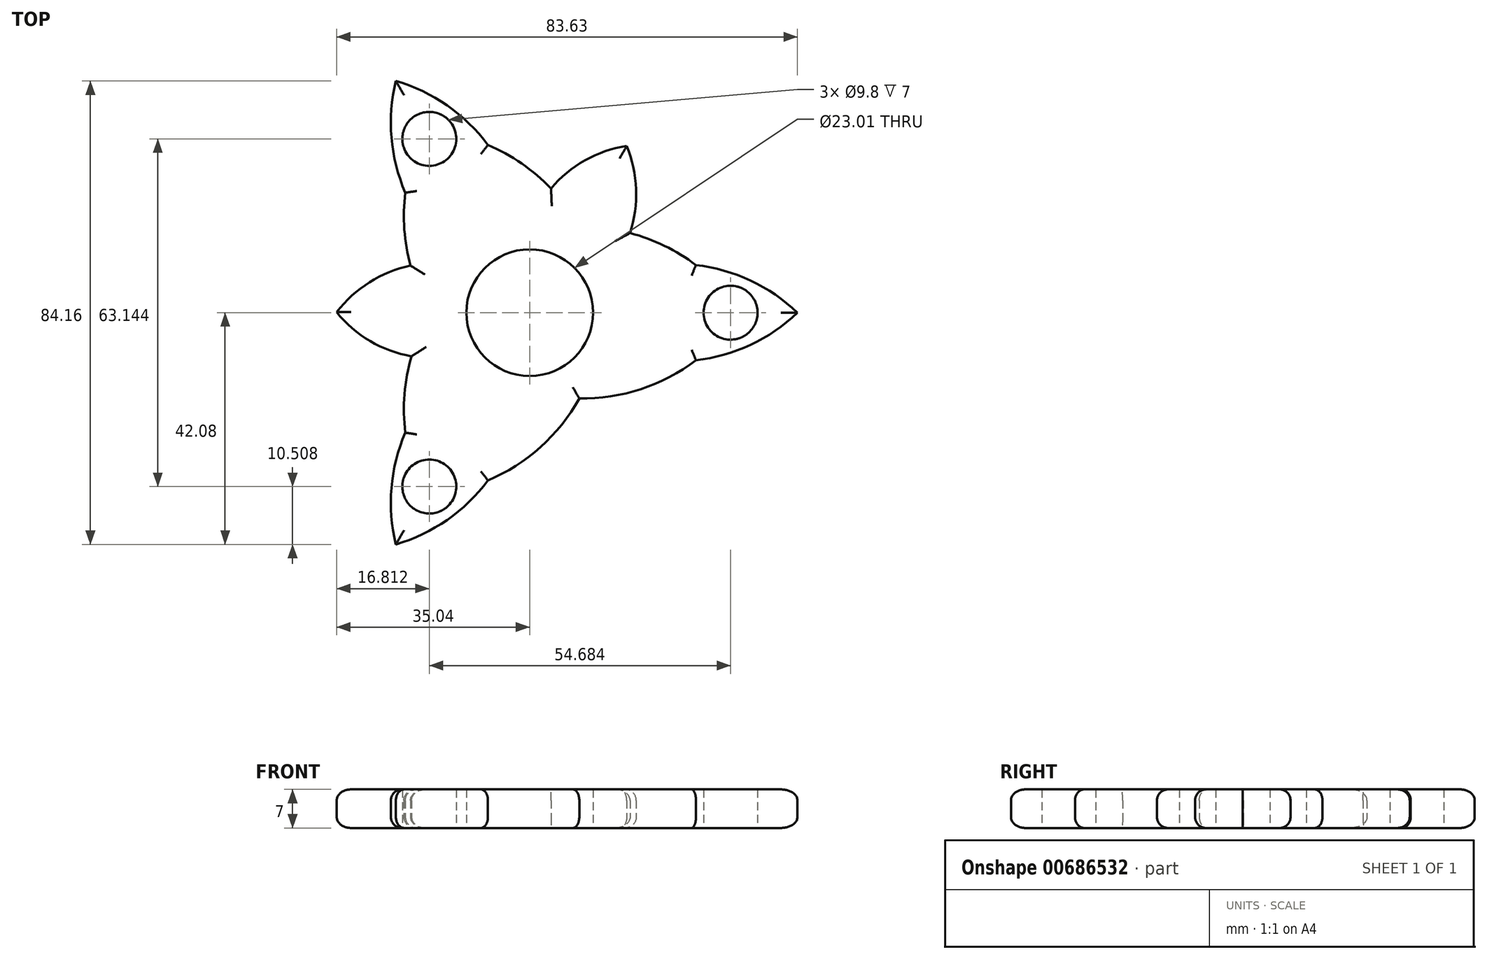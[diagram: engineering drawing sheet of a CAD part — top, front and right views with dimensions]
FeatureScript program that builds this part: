
annotation { "Feature Type Name" : "Feature", "Feature Type Description" : "" }
export const myFeature = defineFeature(function(context is Context, id is Id, definition is map)
    precondition{}
    {
        {
            var Q0;
            Q0=qCreatedBy(makeId("Top.planeOp"),FACE);
            var sketch = newSketch(context, id + "F0", { "sketchPlane" : qUnion([Q0])});
            skCircle(sketch, "E0", {"center": v(0, 0) * mm, "radius": 11.5 * mm});
            skArc(sketch, "E1", {"start": v(30.17, 8.66) * mm, "mid": v(15.75, 15.02) * mm, "end": v(0, 14.24) * mm});
            skArc(sketch, "E2", {"start": v(48.6, 0) * mm, "mid": v(40.09, 5.83) * mm, "end": v(30.17, 8.66) * mm});
            skArc(sketch, "E3.MirrorCS", {"start": v(30.17, -8.66) * mm, "mid": v(15.75, -15.02) * mm, "end": v(0, -14.24) * mm});
            skArc(sketch, "E4.MirrorCS", {"start": v(48.6, 0) * mm, "mid": v(40.09, -5.83) * mm, "end": v(30.17, -8.66) * mm});
            skPoint(sketch, "E5.center", {"position": v(-1.4, 1.63) * mm});
            skArc(sketch, "E6", {"start": v(17.6, 30.3) * mm, "mid": v(8.42, 26.66) * mm, "end": v(1.7, 19.42) * mm});
            skArc(sketch, "E7", {"start": v(17.6, 12.8) * mm, "mid": v(19.33, 21.55) * mm, "end": v(17.6, 30.3) * mm});
            skPoint(sketch, "E8", {"position": v(5.15, 23.94) * mm});
            skPoint(sketch, "E9", {"position": v(18.22, 14.47) * mm});
            skCircle(sketch, "E10", {"center": v(36.46, 0) * mm, "radius": 4.9 * mm});
            skArc(sketch, "E11.1.0", {"start": v(-35.04, 0.1) * mm, "mid": v(-27.3, -6.04) * mm, "end": v(-17.67, -8.25) * mm});
            skArc(sketch, "E11.1.1", {"start": v(-19.89, 8.85) * mm, "mid": v(-28.33, 5.97) * mm, "end": v(-35.04, 0.1) * mm});
            skArc(sketch, "E11.1.2", {"start": v(-22.58, 21.8) * mm, "mid": v(-20.88, 6.13) * mm, "end": v(-12.33, -7.12) * mm});
            skArc(sketch, "E11.1.3", {"start": v(-7.59, 30.46) * mm, "mid": v(5.13, 21.14) * mm, "end": v(12.33, 7.12) * mm});
            skArc(sketch, "E11.1.4", {"start": v(-24.3, 42.08) * mm, "mid": v(-15, 37.63) * mm, "end": v(-7.59, 30.46) * mm});
            skArc(sketch, "E11.1.5", {"start": v(-24.3, 42.08) * mm, "mid": v(-25.1, 31.8) * mm, "end": v(-22.58, 21.8) * mm});
            skCircle(sketch, "E11.1.6", {"center": v(-18.23, 31.57) * mm, "radius": 4.9 * mm});
            skArc(sketch, "E11.2.0", {"start": v(17.43, -30.4) * mm, "mid": v(18.88, -20.62) * mm, "end": v(15.98, -11.18) * mm});
            skArc(sketch, "E11.2.1", {"start": v(2.28, -21.65) * mm, "mid": v(9, -27.52) * mm, "end": v(17.43, -30.4) * mm});
            skArc(sketch, "E11.2.2", {"start": v(-7.59, -30.46) * mm, "mid": v(5.13, -21.14) * mm, "end": v(12.33, -7.12) * mm});
            skArc(sketch, "E11.2.3", {"start": v(-22.58, -21.8) * mm, "mid": v(-20.88, -6.13) * mm, "end": v(-12.33, 7.12) * mm});
            skArc(sketch, "E11.2.4", {"start": v(-24.3, -42.08) * mm, "mid": v(-25.1, -31.8) * mm, "end": v(-22.58, -21.8) * mm});
            skArc(sketch, "E11.2.5", {"start": v(-24.3, -42.08) * mm, "mid": v(-15, -37.63) * mm, "end": v(-7.59, -30.46) * mm});
            skCircle(sketch, "E11.2.6", {"center": v(-18.23, -31.57) * mm, "radius": 4.9 * mm});
            skSolve(sketch);
        }
        {
            var Q0;
            Q0=makeQuery(id+"F0.imprint","IMPRINT",FACE,{"disambiguationData":[TD([[makeQuery(id+"F0.imprint","IMPRINT",EDGE,{"derivedFrom":sQuery(id+"F0.wireOp",EDGE,"E0")}),-1.0]])]});
            var Q1;
            {var subQ0=sQuery(id+"F0.wireOp",EDGE,"E7");var subQ1=sQuery(id+"F0.wireOp",EDGE,"E1");var subQ2=makeQuery(id+"F0.imprint","INTERSECT",VERTEX,{"derivedFrom":[subQ1,subQ0]});Q1=makeQuery(id+"F0.imprint","IMPRINT",FACE,{"disambiguationData":[TD([[makeQuery(id+"F0.imprint","IMPRINT",EDGE,{"disambiguationData":[TD([[subQ2,-1.0]])],"derivedFrom":subQ1}),-1.0]])]});}
            var Q2;
            {var subQ0=sQuery(id+"F0.wireOp",EDGE,"E11.1.1");var subQ1=sQuery(id+"F0.wireOp",EDGE,"E11.1.0");var subQ2=makeQuery(id+"F0.imprint","INTERSECT",VERTEX,{"derivedFrom":[subQ1,subQ0]});Q2=makeQuery(id+"F0.imprint","IMPRINT",FACE,{"disambiguationData":[TD([[makeQuery(id+"F0.imprint","IMPRINT",EDGE,{"disambiguationData":[TD([[subQ2,-1.0]])],"derivedFrom":subQ1}),1.0]])]});}
            var Q3;
            {var subQ0=sQuery(id+"F0.wireOp",EDGE,"E11.2.0");var subQ1=sQuery(id+"F0.wireOp",EDGE,"E3.MirrorCS");var subQ2=makeQuery(id+"F0.imprint","INTERSECT",VERTEX,{"derivedFrom":[subQ1,subQ0]});Q3=makeQuery(id+"F0.imprint","IMPRINT",FACE,{"disambiguationData":[TD([[makeQuery(id+"F0.imprint","IMPRINT",EDGE,{"disambiguationData":[TD([[subQ2,-1.0]])],"derivedFrom":subQ1}),1.0]])]});}
            extrude(context, id + "F1", {"entities" : qUnion([Q0, Q1, Q2, Q3]), "depth" : 7 * mm, "offsetDistance" : 25 * mm});
        }
        {
            var Q0;
            Q0=makeQuery(id+"F1.opExtrude","CAP_EDGE",EDGE,{"disambiguationData":[OSD([sQuery(id+"F0.wireOp",EDGE,"E1")])],"isStart":true});
            var Q1;
            Q1=makeQuery(id+"F1.opExtrude","CAP_EDGE",EDGE,{"disambiguationData":[OSD([sQuery(id+"F0.wireOp",EDGE,"E7")])],"isStart":true});
            var Q2;
            Q2=makeQuery(id+"F1.opExtrude","CAP_EDGE",EDGE,{"disambiguationData":[OSD([sQuery(id+"F0.wireOp",EDGE,"E6")])],"isStart":true});
            var Q3;
            Q3=makeQuery(id+"F1.opExtrude","CAP_EDGE",EDGE,{"disambiguationData":[OSD([sQuery(id+"F0.wireOp",EDGE,"E11.1.3")])],"isStart":true});
            var Q4;
            Q4=makeQuery(id+"F1.opExtrude","CAP_EDGE",EDGE,{"disambiguationData":[OSD([sQuery(id+"F0.wireOp",EDGE,"E11.1.4")])],"isStart":true});
            var Q5;
            Q5=makeQuery(id+"F1.opExtrude","CAP_EDGE",EDGE,{"disambiguationData":[OSD([sQuery(id+"F0.wireOp",EDGE,"E11.1.5")])],"isStart":true});
            var Q6;
            Q6=makeQuery(id+"F1.opExtrude","CAP_EDGE",EDGE,{"disambiguationData":[OSD([sQuery(id+"F0.wireOp",EDGE,"E11.1.2")])],"isStart":true});
            var Q7;
            Q7=makeQuery(id+"F1.opExtrude","CAP_EDGE",EDGE,{"disambiguationData":[OSD([sQuery(id+"F0.wireOp",EDGE,"E11.1.1")])],"isStart":true});
            var Q8;
            Q8=makeQuery(id+"F1.opExtrude","CAP_EDGE",EDGE,{"disambiguationData":[OSD([sQuery(id+"F0.wireOp",EDGE,"E11.1.0")])],"isStart":true});
            var Q9;
            Q9=makeQuery(id+"F1.opExtrude","CAP_EDGE",EDGE,{"disambiguationData":[OSD([sQuery(id+"F0.wireOp",EDGE,"E11.2.3")])],"isStart":true});
            var Q10;
            Q10=makeQuery(id+"F1.opExtrude","CAP_EDGE",EDGE,{"disambiguationData":[OSD([sQuery(id+"F0.wireOp",EDGE,"E11.2.4")])],"isStart":true});
            var Q11;
            Q11=makeQuery(id+"F1.opExtrude","CAP_EDGE",EDGE,{"disambiguationData":[OSD([sQuery(id+"F0.wireOp",EDGE,"E11.2.5")])],"isStart":true});
            var Q12;
            Q12=makeQuery(id+"F1.opExtrude","CAP_EDGE",EDGE,{"disambiguationData":[OSD([sQuery(id+"F0.wireOp",EDGE,"E11.2.2")])],"isStart":true});
            var Q13;
            Q13=makeQuery(id+"F1.opExtrude","CAP_EDGE",EDGE,{"disambiguationData":[OSD([sQuery(id+"F0.wireOp",EDGE,"E11.2.1")])],"isStart":true});
            var Q14;
            Q14=makeQuery(id+"F1.opExtrude","CAP_EDGE",EDGE,{"disambiguationData":[OSD([sQuery(id+"F0.wireOp",EDGE,"E11.2.0")])],"isStart":true});
            var Q15;
            Q15=makeQuery(id+"F1.opExtrude","CAP_EDGE",EDGE,{"disambiguationData":[OSD([sQuery(id+"F0.wireOp",EDGE,"E3.MirrorCS")])],"isStart":true});
            var Q16;
            Q16=makeQuery(id+"F1.opExtrude","CAP_EDGE",EDGE,{"disambiguationData":[OSD([sQuery(id+"F0.wireOp",EDGE,"E4.MirrorCS")])],"isStart":true});
            var Q17;
            Q17=makeQuery(id+"F1.opExtrude","CAP_EDGE",EDGE,{"disambiguationData":[OSD([sQuery(id+"F0.wireOp",EDGE,"E2")])],"isStart":true});
            var Q18;
            Q18=makeQuery(id+"F1.opExtrude","CAP_EDGE",EDGE,{"disambiguationData":[OSD([sQuery(id+"F0.wireOp",EDGE,"E11.1.3")])],"isStart":false});
            var Q19;
            Q19=makeQuery(id+"F1.opExtrude","CAP_EDGE",EDGE,{"disambiguationData":[OSD([sQuery(id+"F0.wireOp",EDGE,"E11.1.4")])],"isStart":false});
            var Q20;
            Q20=makeQuery(id+"F1.opExtrude","CAP_EDGE",EDGE,{"disambiguationData":[OSD([sQuery(id+"F0.wireOp",EDGE,"E11.1.5")])],"isStart":false});
            var Q21;
            Q21=makeQuery(id+"F1.opExtrude","CAP_EDGE",EDGE,{"disambiguationData":[OSD([sQuery(id+"F0.wireOp",EDGE,"E11.1.2")])],"isStart":false});
            var Q22;
            Q22=makeQuery(id+"F1.opExtrude","CAP_EDGE",EDGE,{"disambiguationData":[OSD([sQuery(id+"F0.wireOp",EDGE,"E11.1.1")])],"isStart":false});
            var Q23;
            Q23=makeQuery(id+"F1.opExtrude","CAP_EDGE",EDGE,{"disambiguationData":[OSD([sQuery(id+"F0.wireOp",EDGE,"E11.1.0")])],"isStart":false});
            var Q24;
            Q24=makeQuery(id+"F1.opExtrude","CAP_EDGE",EDGE,{"disambiguationData":[OSD([sQuery(id+"F0.wireOp",EDGE,"E11.2.3")])],"isStart":false});
            var Q25;
            Q25=makeQuery(id+"F1.opExtrude","CAP_EDGE",EDGE,{"disambiguationData":[OSD([sQuery(id+"F0.wireOp",EDGE,"E11.2.4")])],"isStart":false});
            var Q26;
            Q26=makeQuery(id+"F1.opExtrude","CAP_EDGE",EDGE,{"disambiguationData":[OSD([sQuery(id+"F0.wireOp",EDGE,"E11.2.5")])],"isStart":false});
            var Q27;
            Q27=makeQuery(id+"F1.opExtrude","CAP_EDGE",EDGE,{"disambiguationData":[OSD([sQuery(id+"F0.wireOp",EDGE,"E11.2.2")])],"isStart":false});
            var Q28;
            Q28=makeQuery(id+"F1.opExtrude","CAP_EDGE",EDGE,{"disambiguationData":[OSD([sQuery(id+"F0.wireOp",EDGE,"E11.2.1")])],"isStart":false});
            var Q29;
            Q29=makeQuery(id+"F1.opExtrude","CAP_EDGE",EDGE,{"disambiguationData":[OSD([sQuery(id+"F0.wireOp",EDGE,"E11.2.0")])],"isStart":false});
            var Q30;
            Q30=makeQuery(id+"F1.opExtrude","CAP_EDGE",EDGE,{"disambiguationData":[OSD([sQuery(id+"F0.wireOp",EDGE,"E4.MirrorCS")])],"isStart":false});
            var Q31;
            Q31=makeQuery(id+"F1.opExtrude","CAP_EDGE",EDGE,{"disambiguationData":[OSD([sQuery(id+"F0.wireOp",EDGE,"E1")])],"isStart":false});
            var Q32;
            Q32=makeQuery(id+"F1.opExtrude","CAP_EDGE",EDGE,{"disambiguationData":[OSD([sQuery(id+"F0.wireOp",EDGE,"E3.MirrorCS")])],"isStart":false});
            var Q33;
            Q33=makeQuery(id+"F1.opExtrude","CAP_EDGE",EDGE,{"disambiguationData":[OSD([sQuery(id+"F0.wireOp",EDGE,"E2")])],"isStart":false});
            var Q34;
            Q34=makeQuery(id+"F1.opExtrude","CAP_EDGE",EDGE,{"disambiguationData":[OSD([sQuery(id+"F0.wireOp",EDGE,"E6")])],"isStart":false});
            var Q35;
            Q35=makeQuery(id+"F1.opExtrude","CAP_EDGE",EDGE,{"disambiguationData":[OSD([sQuery(id+"F0.wireOp",EDGE,"E7")])],"isStart":false});
            fillet(context, id + "F2", {"entities" : qUnion([Q0, Q1, Q2, Q3, Q4, Q5, Q6, Q7, Q8, Q9, Q10, Q11, Q12, Q13, Q14, Q15, Q16, Q17, Q18, Q19, Q20, Q21, Q22, Q23, Q24, Q25, Q26, Q27, Q28, Q29, Q30, Q31, Q32, Q33, Q34, Q35]), "radius" : 2 * mm, "tangentPropagation" : true, "allowEdgeOverflow" : false});
        }
    });
